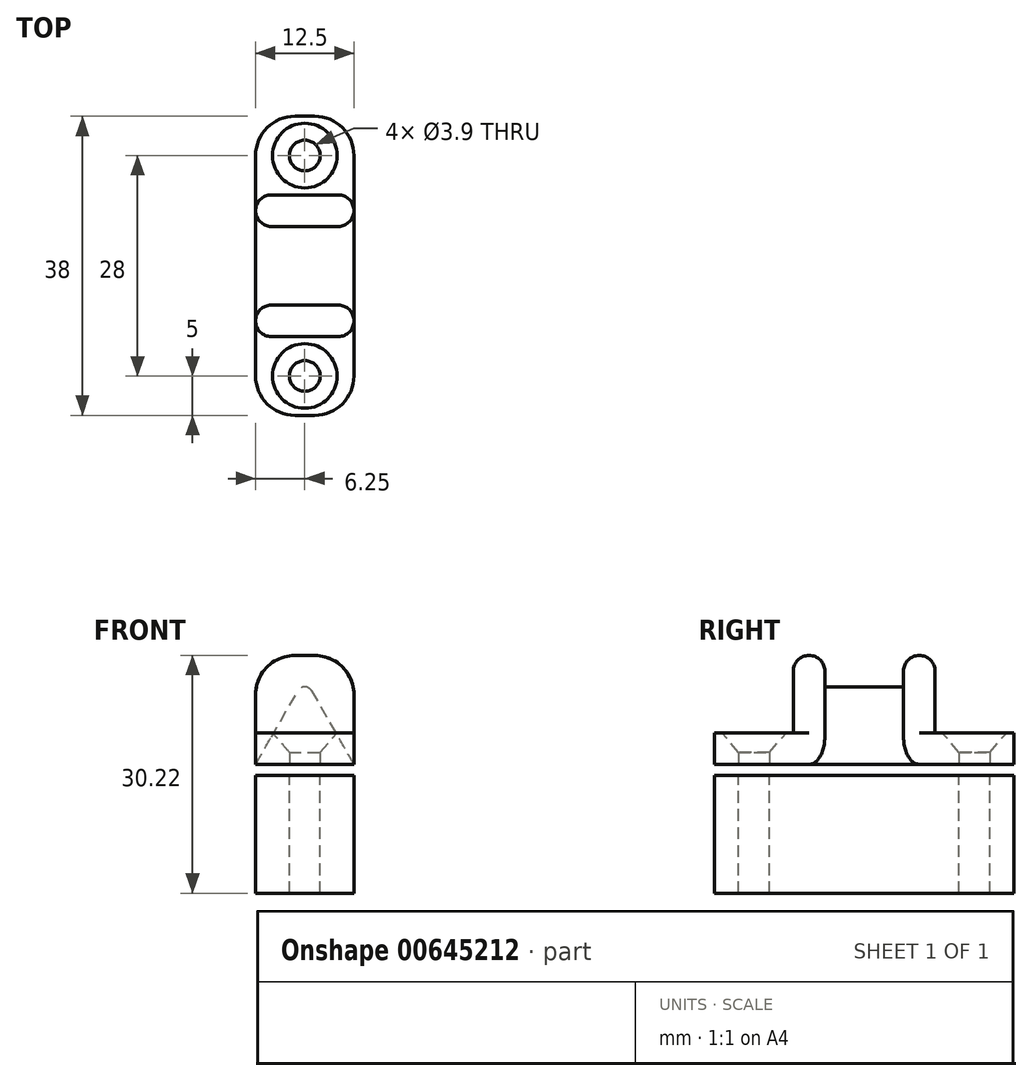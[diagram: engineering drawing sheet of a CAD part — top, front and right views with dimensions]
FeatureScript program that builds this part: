
annotation { "Feature Type Name" : "Feature", "Feature Type Description" : "" }
export const myFeature = defineFeature(function(context is Context, id is Id, definition is map)
    precondition{}
    {
        {
            var Q0;
            Q0=qCreatedBy(makeId("Front.planeOp"),FACE);
            var sketch = newSketch(context, id + "F0", { "sketchPlane" : qUnion([Q0])});
            skCircle(sketch, "E0.cCircle", {"center": v(0, 0) * mm, "radius": 3.6 * mm, "construction": true});
            skLineSegment(sketch, "E0.0", {"start": v(6.25, -3.6) * mm, "end": v(-6.25, -3.6) * mm});
            skLineSegment(sketch, "E0.1", {"start": v(-6.25, -3.6) * mm, "end": v(0, 7.22) * mm});
            skLineSegment(sketch, "E0.2", {"start": v(0, 7.22) * mm, "end": v(6.25, -3.6) * mm});
            skPoint(sketch, "E0.0.midPoint", {"position": v(0, -3.6) * mm});
            skSolve(sketch);
        }
        {
            var Q0;
            Q0=makeQuery(id+"F0.imprint","IMPRINT",FACE,{"disambiguationData":[TD([[makeQuery(id+"F0.imprint","IMPRINT",EDGE,{"derivedFrom":sQuery(id+"F0.wireOp",EDGE,"E0.0")}),-1.0]])]});
            extrude(context, id + "F1", {"entities" : qUnion([Q0]), "depth" : 10 * mm, "offsetDistance" : 25 * mm});
        }
        {
            var Q0;
            Q0=makeQuery(id+"F1.opExtrude","CAP_FACE",FACE,{"disambiguationData":[OSD([sQuery(id+"F0.wireOp",EDGE,"E0.0"),sQuery(id+"F0.wireOp",EDGE,"E0.1"),sQuery(id+"F0.wireOp",EDGE,"E0.2")])],"isStart":false});
            var sketch = newSketch(context, id + "F2", { "sketchPlane" : qUnion([Q0])});
            skLineSegment(sketch, "E1.0", {"start": v(0, 7.22) * mm, "end": v(6.25, -3.6) * mm});
            skLineSegment(sketch, "E1.1", {"start": v(-6.25, -3.6) * mm, "end": v(0, 7.22) * mm});
            skLineSegment(sketch, "E1.2", {"start": v(6.25, -3.6) * mm, "end": v(-6.25, -3.6) * mm});
            skLineSegment(sketch, "E2", {"start": v(-6.25, -3.6) * mm, "end": v(-6.25, 7.22) * mm});
            skLineSegment(sketch, "E3", {"start": v(6.25, -3.6) * mm, "end": v(6.25, 7.22) * mm});
            skLineSegment(sketch, "E4", {"start": v(-6.25, 7.22) * mm, "end": v(-6.25, 10.22) * mm});
            skLineSegment(sketch, "E5", {"start": v(-6.25, 10.22) * mm, "end": v(6.25, 10.22) * mm});
            skLineSegment(sketch, "E6", {"start": v(6.25, 10.22) * mm, "end": v(6.25, 7.22) * mm});
            skSolve(sketch);
        }
        {
            var Q0;
            {var subQ0=sQuery(id+"F2.wireOp",EDGE,"E1.1");Q0=makeQuery(id+"F2.imprint","IMPRINT",FACE,{"disambiguationData":[TD([[makeQuery(id+"F2.imprint","IMPRINT",EDGE,{"derivedFrom":subQ0}),1.0]])]});}
            var Q1;
            {var subQ0=sQuery(id+"F2.wireOp",EDGE,"E1.0");Q1=makeQuery(id+"F2.imprint","IMPRINT",FACE,{"disambiguationData":[TD([[makeQuery(id+"F2.imprint","IMPRINT",EDGE,{"derivedFrom":subQ0}),1.0]])]});}
            var Q2;
            Q2=makeQuery(id+"F2.imprint","IMPRINT",FACE,{"disambiguationData":[TD([[makeQuery(id+"F2.imprint","IMPRINT",EDGE,{"derivedFrom":sQuery(id+"F2.wireOp",EDGE,"E1.0")}),-1.0]])]});
            extrude(context, id + "F3", {"entities" : qUnion([Q0, Q1, Q2]), "operationType" : NewBodyOperationType.ADD, "depth" : 4 * mm, "offsetDistance" : 25 * mm});
        }
        {
            var Q0;
            Q0=makeQuery(id+"F1.opExtrude","CAP_FACE",FACE,{"disambiguationData":[OSD([sQuery(id+"F0.wireOp",EDGE,"E0.0"),sQuery(id+"F0.wireOp",EDGE,"E0.1"),sQuery(id+"F0.wireOp",EDGE,"E0.2")])],"isStart":true});
            var sketch = newSketch(context, id + "F4", { "sketchPlane" : qUnion([Q0])});
            skLineSegment(sketch, "E7.0", {"start": v(-6.25, -3.6) * mm, "end": v(6.25, -3.6) * mm});
            skLineSegment(sketch, "E8.0", {"start": v(0, 7.22) * mm, "end": v(-6.25, -3.6) * mm});
            skLineSegment(sketch, "E8.1", {"start": v(6.25, -3.6) * mm, "end": v(0, 7.22) * mm});
            skLineSegment(sketch, "E9", {"start": v(-6.25, -3.6) * mm, "end": v(-6.25, 7.22) * mm});
            skLineSegment(sketch, "E10", {"start": v(6.25, 7.22) * mm, "end": v(6.25, -3.6) * mm});
            skLineSegment(sketch, "E11.0", {"start": v(6.25, 10.22) * mm, "end": v(-6.25, 10.22) * mm});
            skLineSegment(sketch, "E12", {"start": v(-6.25, 7.22) * mm, "end": v(-6.25, 10.22) * mm});
            skLineSegment(sketch, "E13", {"start": v(6.25, 10.22) * mm, "end": v(6.25, 7.22) * mm});
            skSolve(sketch);
        }
        {
            var Q0;
            {var subQ0=sQuery(id+"F4.wireOp",EDGE,"E8.0");Q0=makeQuery(id+"F4.imprint","IMPRINT",FACE,{"disambiguationData":[TD([[makeQuery(id+"F4.imprint","IMPRINT",EDGE,{"derivedFrom":subQ0}),-1.0]])]});}
            var Q1;
            {var subQ0=sQuery(id+"F4.wireOp",EDGE,"E8.1");Q1=makeQuery(id+"F4.imprint","IMPRINT",FACE,{"disambiguationData":[TD([[makeQuery(id+"F4.imprint","IMPRINT",EDGE,{"derivedFrom":subQ0}),-1.0]])]});}
            var Q2;
            Q2=makeQuery(id+"F4.imprint","IMPRINT",FACE,{"disambiguationData":[TD([[makeQuery(id+"F4.imprint","IMPRINT",EDGE,{"derivedFrom":sQuery(id+"F4.wireOp",EDGE,"E7.0")}),1.0]])]});
            extrude(context, id + "F5", {"entities" : qUnion([Q0, Q1, Q2]), "operationType" : NewBodyOperationType.ADD, "depth" : 4 * mm, "offsetDistance" : 25 * mm});
        }
        {
            var Q0;
            Q0=makeQuery(id+"F5.opExtrude","CAP_FACE",FACE,{"disambiguationData":[OSD([sQuery(id+"F4.wireOp",EDGE,"E7.0"),sQuery(id+"F4.wireOp",EDGE,"E9"),sQuery(id+"F4.wireOp",EDGE,"E10"),sQuery(id+"F4.wireOp",EDGE,"E11.0"),sQuery(id+"F4.wireOp",EDGE,"E12"),sQuery(id+"F4.wireOp",EDGE,"E13")])],"isStart":false});
            var sketch = newSketch(context, id + "F6", { "sketchPlane" : qUnion([Q0])});
            skLineSegment(sketch, "E14.0", {"start": v(-6.25, -3.6) * mm, "end": v(6.25, -3.6) * mm});
            skLineSegment(sketch, "E14.1", {"start": v(6.25, 10.22) * mm, "end": v(6.25, -3.6) * mm});
            skLineSegment(sketch, "E14.2", {"start": v(-6.25, -3.6) * mm, "end": v(-6.25, 10.22) * mm});
            skLineSegment(sketch, "E15", {"start": v(-6.25, 0.4) * mm, "end": v(6.25, 0.4) * mm});
            skSolve(sketch);
        }
        {
            var Q0;
            {var subQ0=sQuery(id+"F6.wireOp",EDGE,"E14.0");Q0=makeQuery(id+"F6.imprint","IMPRINT",FACE,{"disambiguationData":[TD([[makeQuery(id+"F6.imprint","IMPRINT",EDGE,{"derivedFrom":subQ0}),1.0]])]});}
            extrude(context, id + "F7", {"entities" : qUnion([Q0]), "operationType" : NewBodyOperationType.ADD, "depth" : 10 * mm, "offsetDistance" : 25 * mm});
        }
        {
            var Q0;
            Q0=makeQuery(id+"F3.opExtrude","CAP_FACE",FACE,{"disambiguationData":[OSD([sQuery(id+"F2.wireOp",EDGE,"E1.2"),sQuery(id+"F2.wireOp",EDGE,"E2"),sQuery(id+"F2.wireOp",EDGE,"E3"),sQuery(id+"F2.wireOp",EDGE,"E4"),sQuery(id+"F2.wireOp",EDGE,"E5"),sQuery(id+"F2.wireOp",EDGE,"E6")])],"isStart":false});
            var sketch = newSketch(context, id + "F8", { "sketchPlane" : qUnion([Q0])});
            skLineSegment(sketch, "E16.0", {"start": v(6.25, -3.6) * mm, "end": v(-6.25, -3.6) * mm});
            skLineSegment(sketch, "E16.1", {"start": v(6.25, -3.6) * mm, "end": v(6.25, 10.22) * mm});
            skLineSegment(sketch, "E16.2", {"start": v(-6.25, -3.6) * mm, "end": v(-6.25, 10.22) * mm});
            skLineSegment(sketch, "E17.0", {"start": v(6.25, 0.4) * mm, "end": v(-6.25, 0.4) * mm});
            skSolve(sketch);
        }
        {
            var Q0;
            {var subQ0=sQuery(id+"F8.wireOp",EDGE,"E16.0");Q0=makeQuery(id+"F8.imprint","IMPRINT",FACE,{"disambiguationData":[TD([[makeQuery(id+"F8.imprint","IMPRINT",EDGE,{"derivedFrom":subQ0}),-1.0]])]});}
            extrude(context, id + "F9", {"entities" : qUnion([Q0]), "operationType" : NewBodyOperationType.ADD, "depth" : 10 * mm, "offsetDistance" : 25 * mm});
        }
        {
            var Q0;
            Q0=makeQuery(id+"F7.opExtrude","SWEPT_FACE",FACE,{"disambiguationData":[OSD([sQuery(id+"F6.wireOp",EDGE,"E15")])]});
            var sketch = newSketch(context, id + "F10", { "sketchPlane" : qUnion([Q0])});
            skLineSegment(sketch, "E18.0", {"start": v(6.25, 4) * mm, "end": v(-6.25, 4) * mm});
            skLineSegment(sketch, "E18.1", {"start": v(6.25, 14) * mm, "end": v(-6.25, 14) * mm});
            skLineSegment(sketch, "E18.2", {"start": v(6.25, 14) * mm, "end": v(6.25, 4) * mm});
            skLineSegment(sketch, "E18.3", {"start": v(-6.25, 14) * mm, "end": v(-6.25, 4) * mm});
            skLineSegment(sketch, "E18.4", {"start": v(6.25, -14) * mm, "end": v(-6.25, -14) * mm});
            skLineSegment(sketch, "E18.5", {"start": v(6.25, -24) * mm, "end": v(6.25, -14) * mm});
            skLineSegment(sketch, "E18.6", {"start": v(6.25, -24) * mm, "end": v(-6.25, -24) * mm});
            skLineSegment(sketch, "E18.7", {"start": v(-6.25, -24) * mm, "end": v(-6.25, -14) * mm});
            skLineSegment(sketch, "E19", {"start": v(0, 14) * mm, "end": v(0, 4) * mm, "construction": true});
            skLineSegment(sketch, "E20", {"start": v(6.25, 9) * mm, "end": v(-6.25, 9) * mm, "construction": true});
            skLineSegment(sketch, "E21", {"start": v(0, -14) * mm, "end": v(0, -24) * mm, "construction": true});
            skLineSegment(sketch, "E22", {"start": v(6.25, -19) * mm, "end": v(-6.25, -19) * mm, "construction": true});
            skPoint(sketch, "E23", {"position": v(0, 9) * mm});
            skPoint(sketch, "E24", {"position": v(0, -19) * mm});
            skSolve(sketch);
        }
        {
            var Q0;
            Q0=sQuery(id+"F10.wireOp",VERTEX,"E23");
            var Q1;
            Q1=sQuery(id+"F10.wireOp",VERTEX,"E24");
            var Q2;
            Q2=makeQuery(id+"F1.opExtrude","SWEPT_BODY",BODY,{"disambiguationData":[OSD([sQuery(id+"F0.wireOp",EDGE,"E0.0"),sQuery(id+"F0.wireOp",EDGE,"E0.1"),sQuery(id+"F0.wireOp",EDGE,"E0.2")])]});
            hole(context, id + "F11", {"style" : HoleStyle.C_SINK, "endStyle" : HoleEndStyle.THROUGH, "holeDiameter" : 3.9 * mm, "cSinkDiameter" : 8.2 * mm, "cSinkAngle" : 82 * degree, "majorDiameter" : 5 * mm, "isTappedThrough" : true, "tappedDepth" : 12 * mm, "tapClearance" : 3, "locations" : qUnion([Q0, Q1]), "scope" : qUnion([Q2]), "startStyle" : HoleStartStyle.SKETCH});
        }
        {
            var Q0;
            Q0=makeQuery(id+"F7.opExtrude","CAP_EDGE",EDGE,{"disambiguationData":[OSD([sQuery(id+"F6.wireOp",EDGE,"E14.1")])],"isStart":false});
            var Q1;
            Q1=makeQuery(id+"F7.opExtrude","CAP_EDGE",EDGE,{"disambiguationData":[OSD([sQuery(id+"F6.wireOp",EDGE,"E14.2")])],"isStart":false});
            var Q2;
            Q2=makeQuery(id+"F9.opExtrude","CAP_EDGE",EDGE,{"disambiguationData":[OSD([sQuery(id+"F8.wireOp",EDGE,"E16.2")])],"isStart":false});
            var Q3;
            Q3=makeQuery(id+"F9.opExtrude","CAP_EDGE",EDGE,{"disambiguationData":[OSD([sQuery(id+"F8.wireOp",EDGE,"E16.1")])],"isStart":false});
            fillet(context, id + "F12", {"entities" : qUnion([Q0, Q1, Q2, Q3]), "radius" : 5 * mm, "tangentPropagation" : true, "allowEdgeOverflow" : false});
        }
        {
            var Q0;
            Q0=makeQuery(id+"F5.opExtrude","SWEPT_EDGE",EDGE,{"disambiguationData":[OSD([sQuery(id+"F4.wireOp",EDGE,"E11.0"),sQuery(id+"F4.wireOp",EDGE,"E13")])]});
            var Q1;
            Q1=makeQuery(id+"F5.opExtrude","SWEPT_EDGE",EDGE,{"disambiguationData":[OSD([sQuery(id+"F4.wireOp",EDGE,"E11.0"),sQuery(id+"F4.wireOp",EDGE,"E12")])]});
            var Q2;
            Q2=makeQuery(id+"F3.opExtrude","SWEPT_EDGE",EDGE,{"disambiguationData":[OSD([sQuery(id+"F2.wireOp",EDGE,"E5"),sQuery(id+"F2.wireOp",EDGE,"E6")])]});
            var Q3;
            Q3=makeQuery(id+"F3.opExtrude","SWEPT_EDGE",EDGE,{"disambiguationData":[OSD([sQuery(id+"F2.wireOp",EDGE,"E4"),sQuery(id+"F2.wireOp",EDGE,"E5")])]});
            fillet(context, id + "F13", {"entities" : qUnion([Q0, Q1, Q2, Q3]), "radius" : 5 * mm, "tangentPropagation" : true, "allowEdgeOverflow" : false});
        }
        {
            var Q0;
            {var subQ0=sQuery(id+"F2.wireOp",EDGE,"E5");var subQ1=sQuery(id+"F2.wireOp",EDGE,"E4");Q0=makeQuery(id+"F13.opFillet","BLEND_EDGE",EDGE,{"blendedFrom":[makeQuery(id+"F3.opExtrude","SWEPT_EDGE",EDGE,{"disambiguationData":[OSD([subQ1,subQ0])]}),makeQuery(id+"F3.opExtrude","CAP_FACE",FACE,{"disambiguationData":[OSD([sQuery(id+"F2.wireOp",EDGE,"E1.2"),sQuery(id+"F2.wireOp",EDGE,"E2"),sQuery(id+"F2.wireOp",EDGE,"E3"),subQ1,subQ0,sQuery(id+"F2.wireOp",EDGE,"E6")])],"isStart":false})],"blendedInto":[makeQuery(id+"F3.opExtrude","CAP_FACE",FACE,{"disambiguationData":[OSD([sQuery(id+"F2.wireOp",EDGE,"E1.2"),sQuery(id+"F2.wireOp",EDGE,"E2"),sQuery(id+"F2.wireOp",EDGE,"E3"),subQ1,subQ0,sQuery(id+"F2.wireOp",EDGE,"E6")])],"isStart":false})]});}
            var Q1;
            {var subQ0=sQuery(id+"F4.wireOp",EDGE,"E13");var subQ1=sQuery(id+"F4.wireOp",EDGE,"E11.0");Q1=makeQuery(id+"F13.opFillet","BLEND_EDGE",EDGE,{"blendedFrom":[makeQuery(id+"F5.opExtrude","SWEPT_EDGE",EDGE,{"disambiguationData":[OSD([subQ1,subQ0])]}),makeQuery(id+"F5.opExtrude","CAP_FACE",FACE,{"disambiguationData":[OSD([sQuery(id+"F4.wireOp",EDGE,"E7.0"),sQuery(id+"F4.wireOp",EDGE,"E9"),sQuery(id+"F4.wireOp",EDGE,"E10"),subQ1,sQuery(id+"F4.wireOp",EDGE,"E12"),subQ0])],"isStart":false})],"blendedInto":[makeQuery(id+"F5.opExtrude","CAP_FACE",FACE,{"disambiguationData":[OSD([sQuery(id+"F4.wireOp",EDGE,"E7.0"),sQuery(id+"F4.wireOp",EDGE,"E9"),sQuery(id+"F4.wireOp",EDGE,"E10"),subQ1,sQuery(id+"F4.wireOp",EDGE,"E12"),subQ0])],"isStart":false})]});}
            var Q2;
            {var subQ0=sQuery(id+"F4.wireOp",EDGE,"E13");var subQ1=sQuery(id+"F4.wireOp",EDGE,"E11.0");Q2=makeQuery(id+"F13.opFillet","BLEND_EDGE",EDGE,{"blendedFrom":[makeQuery(id+"F5.opExtrude","SWEPT_EDGE",EDGE,{"disambiguationData":[OSD([subQ1,subQ0])]}),makeQuery(id+"F5.opExtrude","CAP_FACE",FACE,{"disambiguationData":[OSD([sQuery(id+"F4.wireOp",EDGE,"E7.0"),sQuery(id+"F4.wireOp",EDGE,"E9"),sQuery(id+"F4.wireOp",EDGE,"E10"),subQ1,sQuery(id+"F4.wireOp",EDGE,"E12"),subQ0])],"isStart":true})],"blendedInto":[makeQuery(id+"F5.opExtrude","CAP_FACE",FACE,{"disambiguationData":[OSD([sQuery(id+"F4.wireOp",EDGE,"E7.0"),sQuery(id+"F4.wireOp",EDGE,"E9"),sQuery(id+"F4.wireOp",EDGE,"E10"),subQ1,sQuery(id+"F4.wireOp",EDGE,"E12"),subQ0])],"isStart":true})]});}
            var Q3;
            {var subQ0=sQuery(id+"F2.wireOp",EDGE,"E5");var subQ1=sQuery(id+"F2.wireOp",EDGE,"E4");Q3=makeQuery(id+"F13.opFillet","BLEND_EDGE",EDGE,{"blendedFrom":[makeQuery(id+"F3.opExtrude","SWEPT_EDGE",EDGE,{"disambiguationData":[OSD([subQ1,subQ0])]}),makeQuery(id+"F3.opExtrude","CAP_FACE",FACE,{"disambiguationData":[OSD([sQuery(id+"F2.wireOp",EDGE,"E1.2"),sQuery(id+"F2.wireOp",EDGE,"E2"),sQuery(id+"F2.wireOp",EDGE,"E3"),subQ1,subQ0,sQuery(id+"F2.wireOp",EDGE,"E6")])],"isStart":true})],"blendedInto":[makeQuery(id+"F3.opExtrude","CAP_FACE",FACE,{"disambiguationData":[OSD([sQuery(id+"F2.wireOp",EDGE,"E1.2"),sQuery(id+"F2.wireOp",EDGE,"E2"),sQuery(id+"F2.wireOp",EDGE,"E3"),subQ1,subQ0,sQuery(id+"F2.wireOp",EDGE,"E6")])],"isStart":true})]});}
            fillet(context, id + "F14", {"entities" : qUnion([Q0, Q1, Q2, Q3]), "radius" : 2 * mm, "tangentPropagation" : true, "allowEdgeOverflow" : false});
        }
        {
            var Q0;
            Q0=makeQuery(id+"F1.opExtrude","SWEPT_EDGE",EDGE,{"disambiguationData":[OSD([sQuery(id+"F0.wireOp",EDGE,"E0.1"),sQuery(id+"F0.wireOp",EDGE,"E0.2")])]});
            fillet(context, id + "F15", {"entities" : qUnion([Q0]), "radius" : 1 * mm, "tangentPropagation" : true, "allowEdgeOverflow" : false});
        }
        {
            var Q0;
            Q0=qCreatedBy(makeId("Top.planeOp"),FACE);
            cPlane(context, id + "F16", {"entities" : qUnion([Q0]), "cplaneType" : CPlaneType.OFFSET, "offset" : 5 * mm, "oppositeDirection" : true, "width" : 150 * mm, "height" : 150 * mm});
        }
        {
            var Q0;
            Q0=qCreatedBy(id+"F16.planeOp",FACE);
            var sketch = newSketch(context, id + "F17", { "sketchPlane" : qUnion([Q0])});
            skLineSegment(sketch, "E25.0.0", {"start": v(1.25, -24) * mm, "end": v(-1.25, -24) * mm});
            skArc(sketch, "E25.0.1", {"start": v(-1.25, -24) * mm, "mid": v(-4.79, -22.54) * mm, "end": v(-6.25, -19) * mm});
            skLineSegment(sketch, "E25.0.2", {"start": v(-6.25, -19) * mm, "end": v(-6.25, -12) * mm});
            skLineSegment(sketch, "E25.0.3", {"start": v(-6.25, -12) * mm, "end": v(-6.25, 2) * mm});
            skLineSegment(sketch, "E25.0.4", {"start": v(-6.25, 2) * mm, "end": v(-6.25, 9) * mm});
            skArc(sketch, "E25.0.5", {"start": v(-6.25, 9) * mm, "mid": v(-4.79, 12.54) * mm, "end": v(-1.25, 14) * mm});
            skLineSegment(sketch, "E25.0.6", {"start": v(-1.25, 14) * mm, "end": v(1.25, 14) * mm});
            skArc(sketch, "E25.0.7", {"start": v(1.25, 14) * mm, "mid": v(4.79, 12.54) * mm, "end": v(6.25, 9) * mm});
            skLineSegment(sketch, "E25.0.8", {"start": v(6.25, 9) * mm, "end": v(6.25, 2) * mm});
            skLineSegment(sketch, "E25.0.9", {"start": v(6.25, 2) * mm, "end": v(6.25, -12) * mm});
            skLineSegment(sketch, "E25.0.10", {"start": v(6.25, -12) * mm, "end": v(6.25, -19) * mm});
            skArc(sketch, "E25.0.11", {"start": v(6.25, -19) * mm, "mid": v(4.79, -22.54) * mm, "end": v(1.25, -24) * mm});
            skLineSegment(sketch, "E26", {"start": v(0, -24) * mm, "end": v(0, 14) * mm, "construction": true});
            skLineSegment(sketch, "E27", {"start": v(6.25, 9) * mm, "end": v(-6.25, 9) * mm, "construction": true});
            skLineSegment(sketch, "E28", {"start": v(6.25, -19) * mm, "end": v(-6.25, -19) * mm, "construction": true});
            skPoint(sketch, "E29", {"position": v(0, -19) * mm});
            skPoint(sketch, "E30", {"position": v(0, 9) * mm});
            skCircle(sketch, "E31.0", {"center": v(0, -19) * mm, "radius": 1.95 * mm});
            skCircle(sketch, "E31.1", {"center": v(0, 9) * mm, "radius": 1.95 * mm});
            skSolve(sketch);
        }
        {
            var Q0;
            Q0=makeQuery(id+"F17.imprint","IMPRINT",FACE,{"disambiguationData":[TD([[makeQuery(id+"F17.imprint","IMPRINT",EDGE,{"derivedFrom":sQuery(id+"F17.wireOp",EDGE,"E25.0.0")}),-1.0]])]});
            extrude(context, id + "F18", {"entities" : qUnion([Q0]), "oppositeDirection" : true, "depth" : 15 * mm, "offsetDistance" : 25 * mm});
        }
    });
